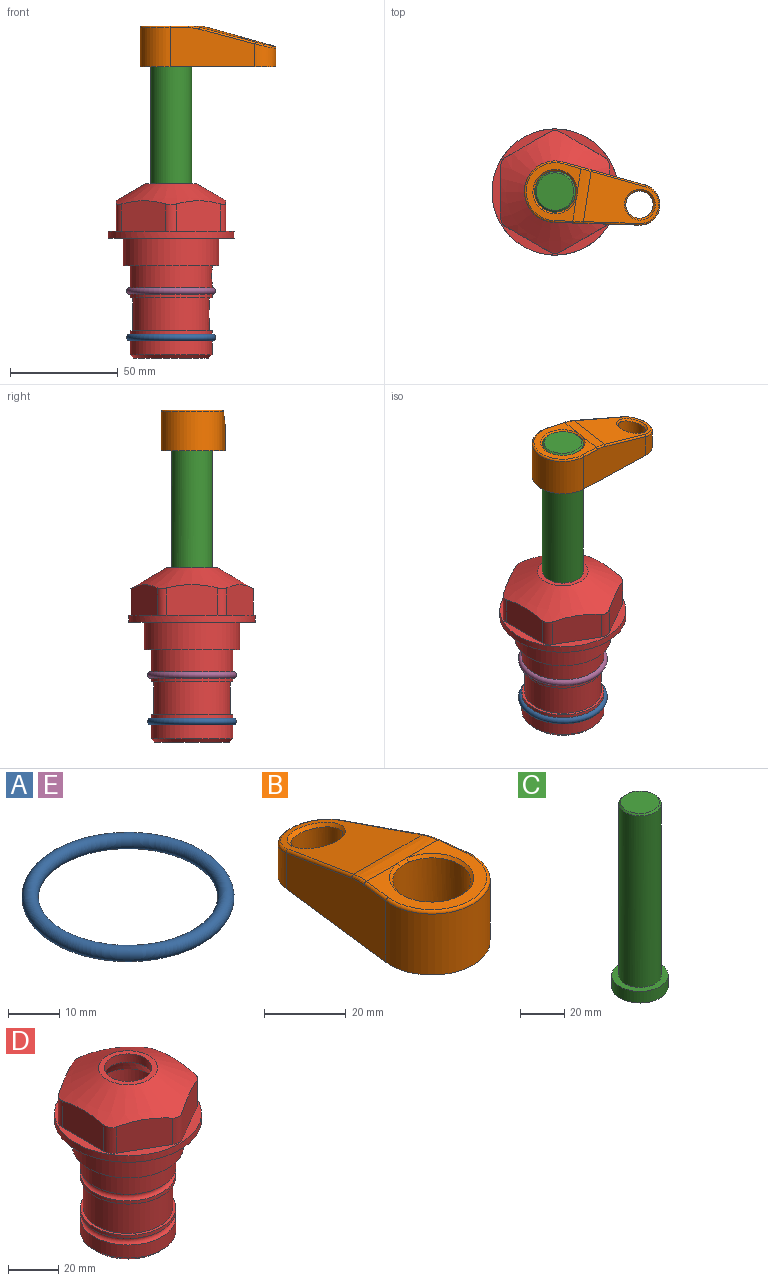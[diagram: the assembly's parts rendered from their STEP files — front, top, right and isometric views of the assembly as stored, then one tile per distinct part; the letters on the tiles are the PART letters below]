
ASSEMBLY  parts=5 mates=4
PART A: 1 faces, bbox 44.7x44.7x3.2 mm
  f0: torus R=19.05mm, axis (0,0,1), area 1193.9mm2
PART B: 31 faces, bbox 31.7x65.5x19.8 mm
  f0: plane 39.12x18.26mm, normal (0.99,0.12,0), area 612.2mm2, adj f1,f4,f7,f11,f13,f15
  f1: cylinder r=9.53mm len=18.91mm, axis (0,0,-1), area 296.1mm2, adj f0,f2,f7,f17
  f2: plane 39.12x18.26mm, normal (-0.99,0.12,0), area 612.2mm2, adj f1,f4,f7,f12,f14,f16
  f3: cylinder r=6.35mm len=12.7mm, axis (0,0,-1), area 362.4mm2, adj f7,f18
  f4: cylinder r=14.29mm len=28.58mm, axis (0,0,-1), area 882.2mm2, adj f0,f2,f7,f10
  f5: cylinder r=9.53mm len=19.05mm, axis (0,0,-1), area 1092.6mm2, adj f7,f19,f20
  f6: plane 26.99x23.69mm, normal (0,0,1), area 216.2mm2, adj f9,f10,f11,f12,f19
  f7: plane 63.5x28.58mm, normal (0,0,-1), area 661.8mm2, adj f0,f1,f2,f3,f4,f5,f22,f23
  f8: plane 33.52x23.6mm, normal (0,0.26,0.97), area 486mm2, adj f9,f15,f16,f17,f18
  f9: cylinder r=19.05mm len=24.72mm, axis (1,0,0), area 120.4mm2, adj f6,f8,f13,f14,f20
  f10: torus R=13.49mm, axis (0,0,1), area 59mm2, adj f4,f6,f11,f12
  f11: cylinder r=0.79mm len=8.67mm, axis (0.12,-0.99,0), area 10.8mm2, adj f0,f6,f10,f13
  f12: cylinder r=0.79mm len=8.67mm, axis (0.12,0.99,0), area 10.8mm2, adj f2,f6,f10,f14
  f13: bspline ~4.95x1.42mm, area 6.1mm2, adj f0,f9,f11,f15
  f14: bspline ~4.95x1.42mm, area 6.1mm2, adj f2,f9,f12,f16
  f15: cylinder r=0.79mm len=25.95mm, axis (0.12,-0.96,0.26), area 32.9mm2, adj f0,f8,f13,f17
  f16: cylinder r=0.79mm len=25.95mm, axis (0.12,0.96,-0.26), area 32.9mm2, adj f2,f8,f14,f17
  f17: bspline ~18.91x8.38mm, area 30mm2, adj f1,f8,f15,f16
  f18: bspline ~14.29x14.29mm, area 48.3mm2, adj f3,f8
  f19: cone r=9.53mm half-angle=45deg, axis (0,0,1), area 66.5mm2, adj f5,f6,f20
  f20: bspline ~3.22x0.96mm, area 3.5mm2, adj f5,f9,f19
  f21: plane 2.75x2.72mm, normal (0,0,-1), area 2.9mm2, adj f23,f25,f28
  f22: plane 23.05x15.88mm, normal (-0.99,-0.12,0), area 323.6mm2, adj f7,f25,f26,f27,f28,f29
  f23: plane 23.05x15.88mm, normal (0.99,-0.12,0), area 323.6mm2, adj f7,f21,f25,f27,f28,f30
  f24: cylinder r=9.53mm len=10.69mm, axis (0,0,-1), area 114.7mm2, adj f7,f27,f29,f30
  f25: cylinder r=12.7mm len=20.59mm, axis (0,0,-1), area 381.1mm2, adj f7,f21,f22,f23,f26,f28
  f26: plane 2.75x2.72mm, normal (0,0,-1), area 2.9mm2, adj f22,f25,f28
  f27: plane 19.72x18.37mm, normal (0,-0.26,-0.97), area 291.8mm2, adj f22,f23,f24,f28,f29,f30
  f28: cylinder r=15.88mm len=19.92mm, axis (1,0,0), area 54.8mm2, adj f21,f22,f23,f25,f26,f27
  f29: cylinder r=1.59mm len=11mm, axis (0,0,-1), area 34.7mm2, adj f7,f22,f24,f27
  f30: cylinder r=1.59mm len=11mm, axis (0,0,-1), area 34.7mm2, adj f7,f23,f24,f27
PART C: 6 faces, bbox 25.4x25.4x101.6 mm
  f0: plane 17.46x17.46mm, normal (0,0,1), area 239.5mm2, adj f5
  f1: plane 25.4x25.4mm, normal (0,0,-1), area 506.7mm2, adj f2
  f2: cylinder r=12.7mm len=25.4mm, axis (0,0,1), area 506.7mm2, adj f1,f3
  f3: plane 25.4x25.4mm, normal (0,0,1), area 221.7mm2, adj f2,f4
  f4: cylinder r=9.53mm len=94.46mm, axis (0,0,1), area 5653mm2, adj f3,f5
  f5: cone r=8.73mm half-angle=45deg, axis (0,0,-1), area 64.4mm2, adj f0,f4
PART D: 36 faces, bbox 58.7x58.7x81 mm
  f0: cylinder r=17.78mm len=35.56mm, axis (0,0,1), area 1670.8mm2, adj f23,f24,f31
  f1: cylinder r=19.05mm len=38.1mm, axis (0,0,1), area 1191.9mm2, adj f26,f27,f30
  f2: plane 58.66x58.66mm, normal (0,0,-1), area 1150.6mm2, adj f3,f28
  f3: cylinder r=29.33mm len=58.66mm, axis (0,0,-1), area 585.1mm2, adj f2,f4
  f4: plane 58.66x58.66mm, normal (0,0,1), area 475.9mm2, adj f3,f5,f6,f7,f8,f9,f10,f11
  f5: plane 20.32x14.34mm, normal (-0.5,0.87,0), area 324.4mm2, adj f4,f15,f16,f17
  f6: plane 20.32x14.34mm, normal (0.5,0.87,0), area 324.4mm2, adj f4,f14,f15,f17
  f7: plane 23.48x14.34mm, normal (1,0,0), area 324.4mm2, adj f4,f13,f14,f17
  f8: plane 20.32x14.34mm, normal (0.5,-0.87,0), area 324.4mm2, adj f4,f12,f13,f17
  f9: plane 20.32x14.34mm, normal (-0.5,-0.87,0), area 324.4mm2, adj f4,f11,f12,f17
  f10: plane 23.48x14.34mm, normal (-1,0,0), area 324.4mm2, adj f4,f11,f16,f17
  f11: cylinder r=5.08mm len=12.85mm, axis (0,0,-1), area 67.2mm2, adj f4,f9,f10,f17
  f12: cylinder r=5.08mm len=12.85mm, axis (0,0,-1), area 67.2mm2, adj f4,f8,f9,f17
  f13: cylinder r=5.08mm len=12.85mm, axis (0,0,-1), area 67.2mm2, adj f4,f7,f8,f17
  f14: cylinder r=5.08mm len=12.85mm, axis (0,0,-1), area 67.2mm2, adj f4,f6,f7,f17
  f15: cylinder r=5.08mm len=12.85mm, axis (0,0,-1), area 67.2mm2, adj f4,f5,f6,f17
  f16: cylinder r=5.08mm len=12.85mm, axis (0,0,-1), area 67.2mm2, adj f4,f5,f10,f17
  f17: cone r=11.73mm half-angle=60deg, axis (0,0,-1), area 2071.8mm2, adj f5,f6,f7,f8,f9,f10,f11,f12
  f18: plane 23.46x23.46mm, normal (0,0,1), area 147.4mm2, adj f17,f35
  f19: plane 34.93x34.93mm, normal (0,0,-1), area 958mm2, adj f29
  f20: cylinder r=19.05mm len=38.1mm, axis (0,0,1), area 760.1mm2, adj f21,f29
  f21: torus R=19.05mm, axis (0,0,1), area 565.3mm2, adj f20,f22
  f22: cylinder r=19.05mm len=38.1mm, axis (0,0,1), area 190mm2, adj f21,f23
  f23: plane 38.1x38.1mm, normal (0,0,1), area 146.9mm2, adj f0,f22
  f24: plane 38.1x38.1mm, normal (0,0,-1), area 146.9mm2, adj f0,f25
  f25: cylinder r=19.05mm len=38.1mm, axis (0,0,1), area 190mm2, adj f24,f26
  f26: torus R=19.05mm, axis (0,0,1), area 565.3mm2, adj f1,f25
  f27: plane 44.45x44.45mm, normal (0,0,-1), area 411.7mm2, adj f1,f28
  f28: cylinder r=22.23mm len=44.45mm, axis (0,0,1), area 1773.5mm2, adj f2,f27
  f29: cone r=19.05mm half-angle=45deg, axis (0,0,1), area 257.5mm2, adj f19,f20
  f30: cylinder r=3.17mm len=6.75mm, axis (-1,0,0), area 128mm2, adj f1,f33
  f31: cylinder r=3.17mm len=6.35mm, axis (-1,0,0), area 102.5mm2, adj f0,f33
  f32: plane 25.4x25.4mm, normal (0,0,1), area 506.7mm2, adj f33
  f33: cylinder r=12.7mm len=66.42mm, axis (0,0,-1), area 5236.2mm2, adj f30,f31,f32,f34
  f34: cone r=9.53mm half-angle=30deg, axis (0,0,-1), area 443.4mm2, adj f33,f35
  f35: cylinder r=9.53mm len=19.05mm, axis (0,0,-1), area 240.9mm2, adj f18,f34
PART E: same geometry as A
PLACE A t=(0,0,-21.59)mm
PLACE B rot(axis=(0,0,-1),98.7deg) t=(0,0,35.17)mm
PLACE C rot(axis=(0,0,-1),98.7deg) t=(0,0,35.17)mm
PLACE D at identity fixed
PLACE E at identity
MATE cylindrical C.f2 <-> D.f0  axis (0,0,-1) through (0,0,-2.93)mm
MATE fastened A.f0 <-> D.f0  axis (0,0,1) through (0,0,-46.1)mm
MATE fastened E.f0 <-> D.f0  axis (0,0,1) through (0,0,-24.51)mm
MATE fastened C.f2 <-> B.f4  axis (0,0,-1) through (0,0,97.88)mm
